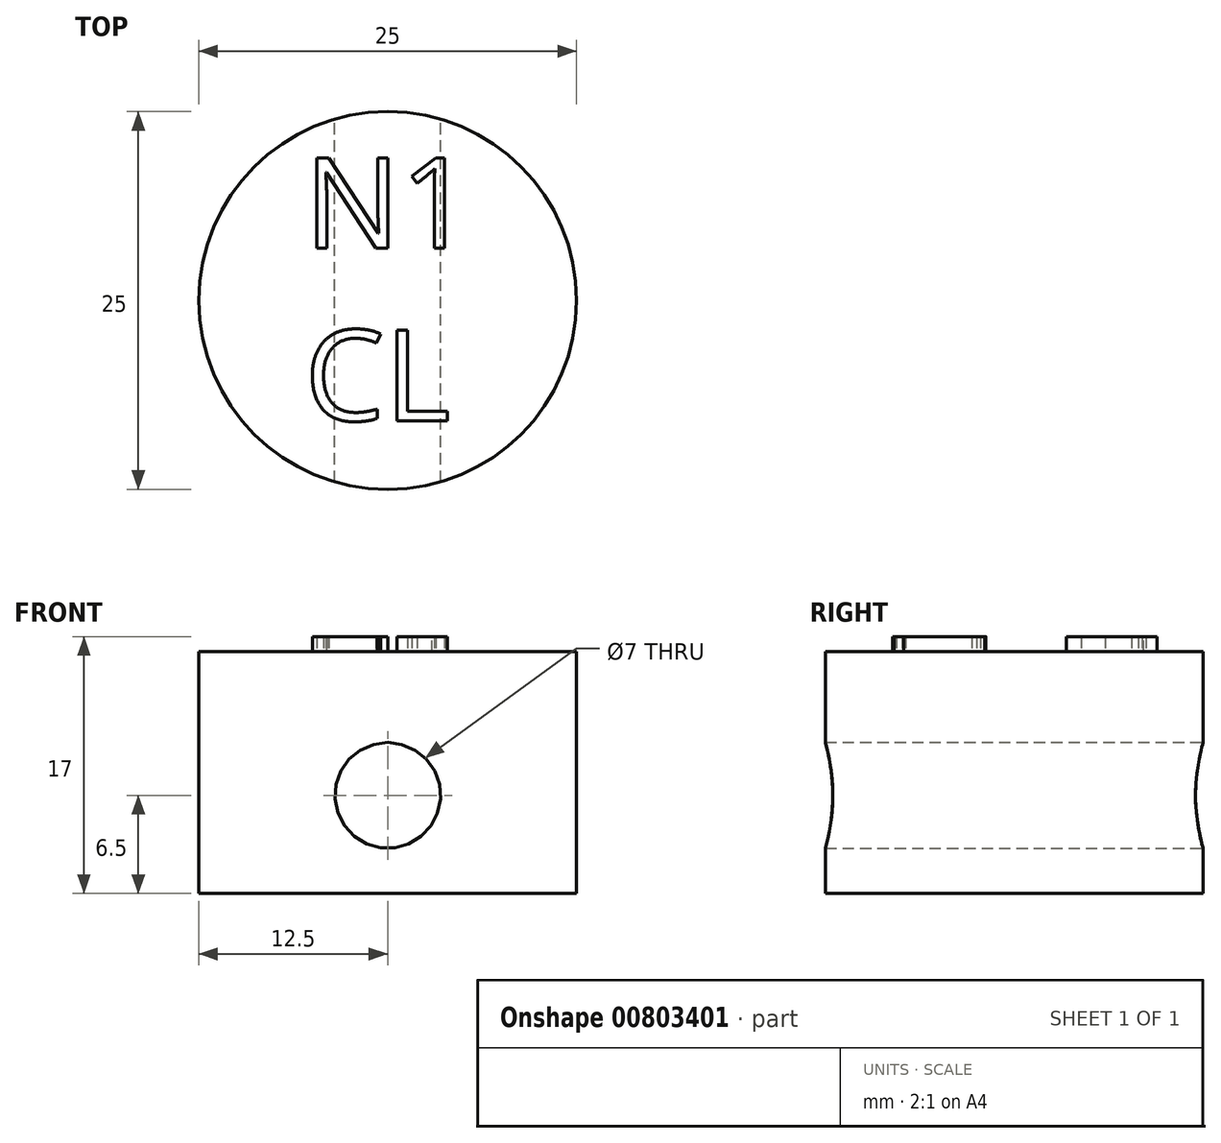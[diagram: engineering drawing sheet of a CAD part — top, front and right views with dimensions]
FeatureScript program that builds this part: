
annotation { "Feature Type Name" : "Feature", "Feature Type Description" : "" }
export const myFeature = defineFeature(function(context is Context, id is Id, definition is map)
    precondition{}
    {
        {
            var Q0;
            Q0=qCreatedBy(makeId("Top.planeOp"),FACE);
            var sketch = newSketch(context, id + "F0", { "sketchPlane" : qUnion([Q0])});
            skCircle(sketch, "E0", {"center": v(0, 0) * mm, "radius": 12.5 * mm});
            skSolve(sketch);
        }
        {
            var Q0;
            Q0=qSketchRegion(id+"F0",true);
            extrude(context, id + "F1", {"entities" : qUnion([Q0]), "depth" : 16 * mm, "offsetDistance" : 25 * mm});
        }
        {
            var Q0;
            Q0=qCreatedBy(makeId("Front.planeOp"),FACE);
            cPlane(context, id + "F2", {"entities" : qUnion([Q0]), "cplaneType" : CPlaneType.OFFSET, "offset" : 12.5 * mm, "oppositeDirection" : true, "width" : 150 * mm, "height" : 150 * mm});
        }
        {
            var Q0;
            Q0=qCreatedBy(id+"F2.planeOp",FACE);
            var sketch = newSketch(context, id + "F3", { "sketchPlane" : qUnion([Q0])});
            skLineSegment(sketch, "E1", {"start": v(0, 0) * mm, "end": v(0, 16) * mm, "construction": true});
            skPoint(sketch, "E2", {"position": v(0, 6.5) * mm});
            skCircle(sketch, "E3", {"center": v(0, 6.5) * mm, "radius": 3.5 * mm});
            skSolve(sketch);
        }
        {
            var Q0;
            Q0=makeQuery(id+"F3.imprint","IMPRINT",FACE,{"disambiguationData":[TD([[makeQuery(id+"F3.imprint","IMPRINT",EDGE,{"derivedFrom":sQuery(id+"F3.wireOp",EDGE,"E3")}),1.0]])]});
            extrude(context, id + "F4", {"entities" : qUnion([Q0]), "operationType" : NewBodyOperationType.REMOVE, "endBound" : BoundingType.THROUGH_ALL, "depth" : 25 * mm, "offsetDistance" : 25 * mm});
        }
        {
            var Q0;
            Q0=makeQuery(id+"F1.opExtrude","CAP_FACE",FACE,{"disambiguationData":[OSD([sQuery(id+"F0.wireOp",EDGE,"E0")])],"isStart":false});
            var sketch = newSketch(context, id + "F5", { "sketchPlane" : qUnion([Q0])});
            skText(sketch, "E4", { "text": "N1\nCL", "fontName": "OpenSans-Regular.ttf"});
            skPoint(sketch, "E5", {"position": v(0, 12.5) * mm});
            skPoint(sketch, "E6", {"position": v(-12.5, 0) * mm});
            const initialGuessF5  = {"E4": [-0.0055, 0.00346, 1, 0, 0.00604]};
            skSetInitialGuess(sketch, initialGuessF5);
            skSolve(sketch);
        }
        {
            var Q0;
            Q0=qSketchRegion(id+"F5",true);
            extrude(context, id + "F6", {"entities" : qUnion([Q0]), "operationType" : NewBodyOperationType.ADD, "depth" : 1 * mm, "offsetDistance" : 25 * mm});
        }
    });
